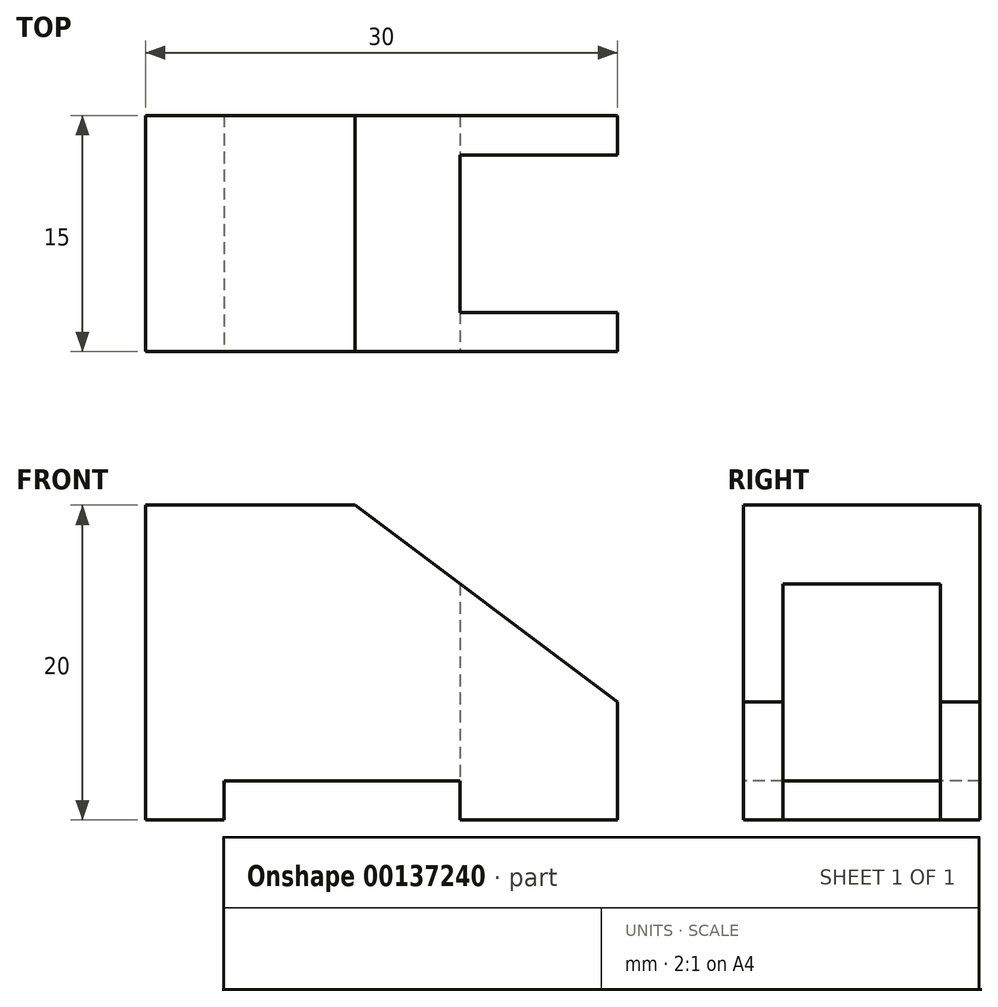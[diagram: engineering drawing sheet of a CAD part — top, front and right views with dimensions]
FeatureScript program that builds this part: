
annotation { "Feature Type Name" : "Feature", "Feature Type Description" : "" }
export const myFeature = defineFeature(function(context is Context, id is Id, definition is map)
    precondition{}
    {
        {
            var Q0;
            Q0=qCreatedBy(makeId("Front.planeOp"),FACE);
            var sketch = newSketch(context, id + "F0", { "sketchPlane" : qUnion([Q0])});
            skLineSegment(sketch, "E0.bottom", {"start": v(0, 0) * mm, "end": v(30, 0) * mm});
            skLineSegment(sketch, "E0.top", {"start": v(0, 20) * mm, "end": v(30, 20) * mm});
            skLineSegment(sketch, "E0.left", {"start": v(0, 0) * mm, "end": v(0, 20) * mm});
            skLineSegment(sketch, "E0.right", {"start": v(30, 0) * mm, "end": v(30, 20) * mm});
            skSolve(sketch);
        }
        {
            var Q0;
            Q0 = qSketchRegion(id + "F0", true);
            extrude(context, id + "F1", {"entities" : qUnion([Q0]), "depth" : 15 * mm});
        }
        {
            var Q0;
            Q0=makeQuery(id+"F1.opExtrude","CAP_FACE",FACE,{"disambiguationData":[OSD([sQuery(id+"F0.wireOp",EDGE,"E0.bottom"),sQuery(id+"F0.wireOp",EDGE,"E0.top"),sQuery(id+"F0.wireOp",EDGE,"E0.left"),sQuery(id+"F0.wireOp",EDGE,"E0.right")])],"isStart":false});
            var sketch = newSketch(context, id + "F2", { "sketchPlane" : qUnion([Q0])});
            skLineSegment(sketch, "E1.bottom", {"start": v(5, 0) * mm, "end": v(20, 0) * mm});
            skLineSegment(sketch, "E1.top", {"start": v(5, 2.5) * mm, "end": v(20, 2.5) * mm});
            skLineSegment(sketch, "E1.left", {"start": v(5, 0) * mm, "end": v(5, 2.5) * mm});
            skLineSegment(sketch, "E1.right", {"start": v(20, 0) * mm, "end": v(20, 2.5) * mm});
            skLineSegment(sketch, "E2", {"start": v(30, 20) * mm, "end": v(13.33, 20) * mm});
            skLineSegment(sketch, "E3", {"start": v(30, 20) * mm, "end": v(30, 7.5) * mm});
            skLineSegment(sketch, "E4", {"start": v(13.33, 20) * mm, "end": v(30, 7.5) * mm});
            skSolve(sketch);
        }
        {
            var Q0;
            Q0 = qSketchRegion(id + "F2", true);
            extrude(context, id + "F3", {"entities" : qUnion([Q0]), "operationType" : NewBodyOperationType.REMOVE, "endBound" : BoundingType.THROUGH_ALL, "oppositeDirection" : true, "depth" : 25 * mm});
        }
        {
            var Q0;
            Q0=makeQuery(id+"F1.opExtrude","SWEPT_FACE",FACE,{"disambiguationData":[OSD([sQuery(id+"F0.wireOp",EDGE,"E0.bottom")])]});
            var sketch = newSketch(context, id + "F4", { "sketchPlane" : qUnion([Q0])});
            skLineSegment(sketch, "E5.bottom", {"start": v(30, 12.5) * mm, "end": v(20, 12.5) * mm});
            skLineSegment(sketch, "E5.top", {"start": v(30, 2.5) * mm, "end": v(20, 2.5) * mm});
            skLineSegment(sketch, "E5.left", {"start": v(30, 12.5) * mm, "end": v(30, 2.5) * mm});
            skLineSegment(sketch, "E5.right", {"start": v(20, 12.5) * mm, "end": v(20, 2.5) * mm});
            skSolve(sketch);
        }
        {
            var Q0;
            Q0 = qSketchRegion(id + "F4", true);
            extrude(context, id + "F5", {"entities" : qUnion([Q0]), "operationType" : NewBodyOperationType.REMOVE, "endBound" : BoundingType.THROUGH_ALL, "oppositeDirection" : true, "depth" : 25 * mm});
        }
    });
